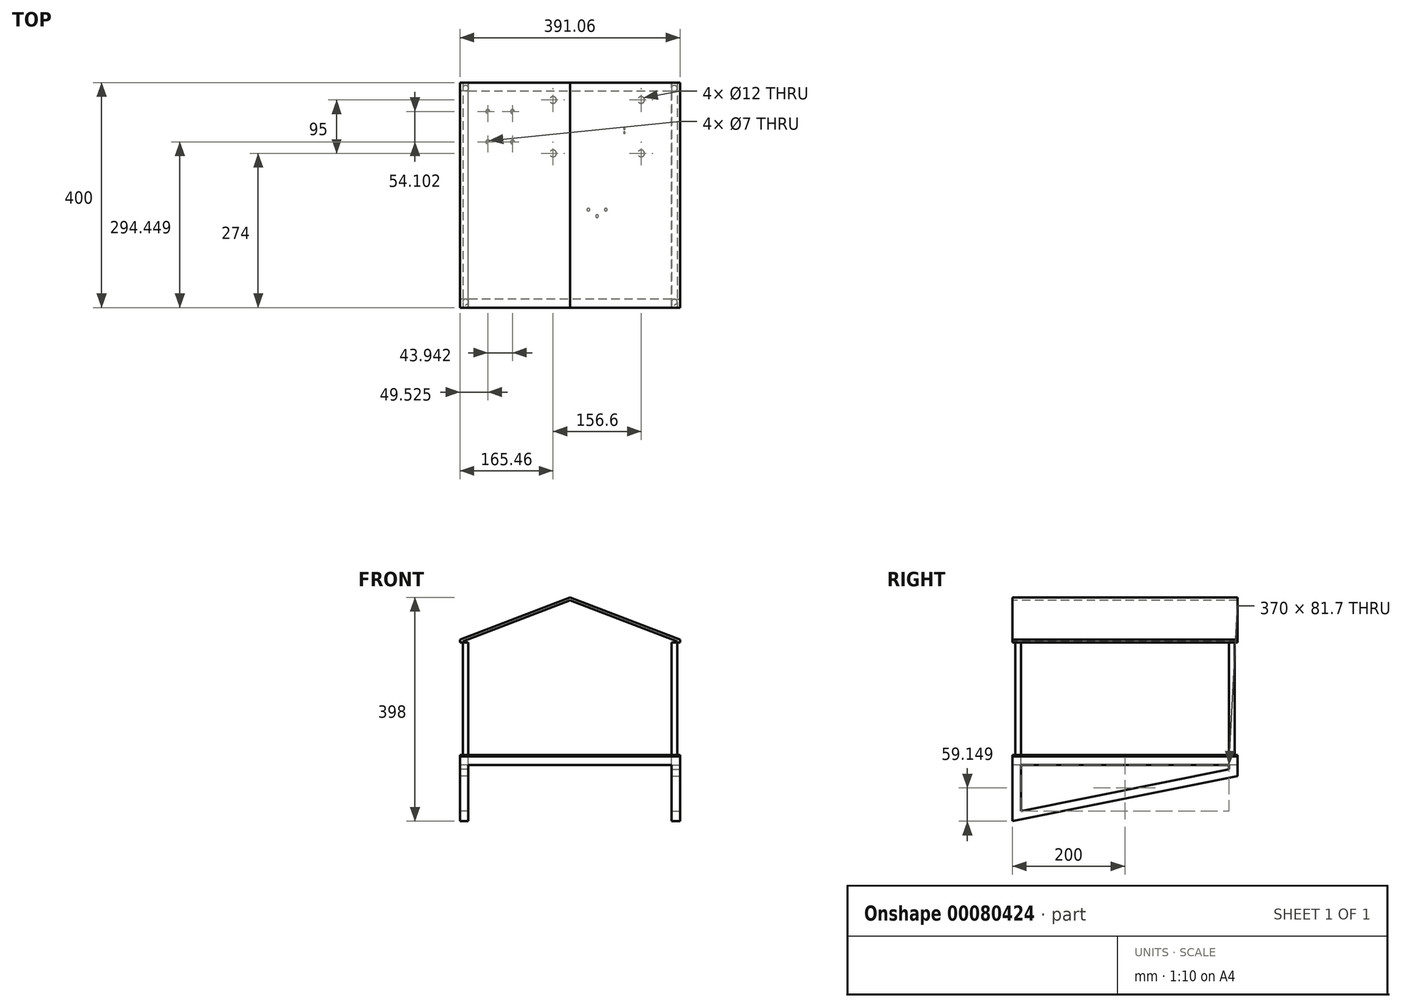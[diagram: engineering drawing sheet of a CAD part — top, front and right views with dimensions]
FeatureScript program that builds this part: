
annotation { "Feature Type Name" : "Feature", "Feature Type Description" : "" }
export const myFeature = defineFeature(function(context is Context, id is Id, definition is map)
    precondition{}
    {
        {
            var Q0;
            Q0=qCreatedBy(makeId("Top.planeOp"),FACE);
            var sketch = newSketch(context, id + "F0", { "sketchPlane" : qUnion([Q0])});
            skLineSegment(sketch, "E0.bottom", {"start": v(-195.53, 200) * mm, "end": v(195.53, 200) * mm});
            skLineSegment(sketch, "E0.top", {"start": v(-195.53, -200) * mm, "end": v(195.53, -200) * mm});
            skLineSegment(sketch, "E0.left", {"start": v(-195.53, 200) * mm, "end": v(-195.53, -200) * mm});
            skLineSegment(sketch, "E0.right", {"start": v(195.53, 200) * mm, "end": v(195.53, -200) * mm});
            skPoint(sketch, "E0.middle", {"position": v(0, 0) * mm});
            skCircle(sketch, "E1", {"center": v(126.53, 169) * mm, "radius": 6 * mm});
            skCircle(sketch, "E2", {"center": v(126.53, 74) * mm, "radius": 6 * mm});
            skLineSegment(sketch, "E3", {"start": v(48.23, 169) * mm, "end": v(48.23, 74) * mm, "construction": true});
            skCircle(sketch, "E4.MirrorC", {"center": v(-30.07, 169) * mm, "radius": 6 * mm});
            skCircle(sketch, "E5.MirrorC", {"center": v(-30.07, 74) * mm, "radius": 6 * mm});
            skLineSegment(sketch, "E6.bottom", {"start": v(107.53, 185) * mm, "end": v(145.53, 185) * mm, "construction": true});
            skLineSegment(sketch, "E6.top", {"start": v(107.53, 58) * mm, "end": v(145.53, 58) * mm, "construction": true});
            skLineSegment(sketch, "E6.left", {"start": v(107.53, 185) * mm, "end": v(107.53, 58) * mm, "construction": true});
            skLineSegment(sketch, "E6.right", {"start": v(145.53, 185) * mm, "end": v(145.53, 58) * mm, "construction": true});
            skPoint(sketch, "E6.middle", {"position": v(126.53, 121.5) * mm});
            skLineSegment(sketch, "E7", {"start": v(126.53, 169) * mm, "end": v(126.53, 74) * mm, "construction": true});
            skCircle(sketch, "E8", {"center": v(-102.06, 148.55) * mm, "radius": 3.5 * mm});
            skCircle(sketch, "E9", {"center": v(-102.06, 94.45) * mm, "radius": 3.5 * mm});
            skLineSegment(sketch, "E10", {"start": v(-124.03, 148.55) * mm, "end": v(-124.03, 94.45) * mm, "construction": true});
            skCircle(sketch, "E11.MirrorC", {"center": v(-146, 148.55) * mm, "radius": 3.5 * mm});
            skCircle(sketch, "E12.MirrorC", {"center": v(-146, 94.45) * mm, "radius": 3.5 * mm});
            skPoint(sketch, "E13", {"position": v(-124.03, 121.5) * mm});
            skLineSegment(sketch, "E14.bottom", {"start": v(-155.53, 161.5) * mm, "end": v(-92.54, 161.5) * mm, "construction": true});
            skLineSegment(sketch, "E14.top", {"start": v(-155.53, 81.5) * mm, "end": v(-92.54, 81.5) * mm, "construction": true});
            skLineSegment(sketch, "E14.left", {"start": v(-155.53, 161.5) * mm, "end": v(-155.53, 81.5) * mm, "construction": true});
            skLineSegment(sketch, "E14.right", {"start": v(-92.54, 161.5) * mm, "end": v(-92.54, 81.5) * mm, "construction": true});
            skCircle(sketch, "E15", {"center": v(32.73, -25.91) * mm, "radius": 2.5 * mm});
            skCircle(sketch, "E16", {"center": v(63.73, -25.91) * mm, "radius": 2.5 * mm});
            skLineSegment(sketch, "E17", {"start": v(32.73, -25.91) * mm, "end": v(63.73, -25.91) * mm, "construction": true});
            skPoint(sketch, "E18", {"position": v(48.23, -25.91) * mm});
            skCircle(sketch, "E19", {"center": v(48.23, -37.5) * mm, "radius": 1.59 * mm, "construction": true});
            skPoint(sketch, "E20", {"position": v(48.23, -35.91) * mm});
            skCircle(sketch, "E21", {"center": v(48.23, -37.5) * mm, "radius": 2.5 * mm});
            skLineSegment(sketch, "E22.bottom", {"start": v(94.23, 122) * mm, "end": v(99.23, 122) * mm, "construction": true});
            skLineSegment(sketch, "E22.top", {"start": v(94.23, 107) * mm, "end": v(99.23, 107) * mm, "construction": true});
            skLineSegment(sketch, "E22.left", {"start": v(94.23, 122) * mm, "end": v(94.23, 107) * mm, "construction": true});
            skLineSegment(sketch, "E22.right", {"start": v(99.23, 122) * mm, "end": v(99.23, 121) * mm, "construction": true});
            skLineSegment(sketch, "E23", {"start": v(94.23, 121) * mm, "end": v(99.23, 121) * mm, "construction": true});
            skLineSegment(sketch, "E24", {"start": v(99.23, 121) * mm, "end": v(99.23, 107) * mm, "construction": true});
            skPoint(sketch, "E25", {"position": v(99.23, 121.5) * mm});
            skCircle(sketch, "E26", {"center": v(96.73, 118) * mm, "radius": 1.5 * mm});
            skPoint(sketch, "E26.centerSnap0", {"position": v(96.73, 122) * mm});
            skCircle(sketch, "E27", {"center": v(96.73, 111) * mm, "radius": 1.5 * mm});
            skLineSegment(sketch, "E28", {"start": v(96.73, 118) * mm, "end": v(96.73, 111) * mm, "construction": true});
            skPoint(sketch, "E29", {"position": v(94.23, 114.5) * mm});
            skPoint(sketch, "E30", {"position": v(96.73, 114.5) * mm});
            skSolve(sketch);
        }
        {
            var Q0;
            Q0 = qSketchRegion(id + "F0", true);
            extrude(context, id + "F1", {"entities" : qUnion([Q0]), "endBound" : BoundingType.SYMMETRIC, "depth" : 3 * mm});
        }
        {
            var Q0;
            Q0=makeQuery(id+"F1.opExtrude","CAP_FACE",FACE,{"disambiguationData":[OSD([sQuery(id+"F0.wireOp",EDGE,"E0.bottom"),sQuery(id+"F0.wireOp",EDGE,"E0.top"),sQuery(id+"F0.wireOp",EDGE,"E0.left"),sQuery(id+"F0.wireOp",EDGE,"E0.right"),sQuery(id+"F0.wireOp",EDGE,"E1"),sQuery(id+"F0.wireOp",EDGE,"E2"),sQuery(id+"F0.wireOp",EDGE,"E4.MirrorC"),sQuery(id+"F0.wireOp",EDGE,"E5.MirrorC"),sQuery(id+"F0.wireOp",EDGE,"E8"),sQuery(id+"F0.wireOp",EDGE,"E9"),sQuery(id+"F0.wireOp",EDGE,"E11.MirrorC"),sQuery(id+"F0.wireOp",EDGE,"E12.MirrorC"),sQuery(id+"F0.wireOp",EDGE,"E15"),sQuery(id+"F0.wireOp",EDGE,"E16"),sQuery(id+"F0.wireOp",EDGE,"E21"),sQuery(id+"F0.wireOp",EDGE,"E26"),sQuery(id+"F0.wireOp",EDGE,"E27")])],"isStart":true});
            var sketch = newSketch(context, id + "F2", { "sketchPlane" : qUnion([Q0])});
            skLineSegment(sketch, "E31.0.0", {"start": v(-195.53, -200) * mm, "end": v(195.53, -200) * mm});
            skLineSegment(sketch, "E31.0.1", {"start": v(195.53, -200) * mm, "end": v(195.53, 200) * mm});
            skLineSegment(sketch, "E31.0.2", {"start": v(195.53, 200) * mm, "end": v(-195.53, 200) * mm});
            skLineSegment(sketch, "E31.0.3", {"start": v(-195.53, 200) * mm, "end": v(-195.53, -200) * mm});
            skLineSegment(sketch, "E32.0", {"start": v(-180.53, -185) * mm, "end": v(180.53, -185) * mm});
            skLineSegment(sketch, "E32.1", {"start": v(-180.53, 185) * mm, "end": v(-180.53, -185) * mm});
            skLineSegment(sketch, "E32.2", {"start": v(180.53, 185) * mm, "end": v(-180.53, 185) * mm});
            skLineSegment(sketch, "E32.3", {"start": v(180.53, -185) * mm, "end": v(180.53, 185) * mm});
            skSolve(sketch);
        }
        {
            var Q0;
            Q0 = qSketchRegion(id + "F2", true);
            extrude(context, id + "F3", {"entities" : qUnion([Q0]), "depth" : 15 * mm});
        }
        {
            var Q0;
            Q0=makeQuery(id+"F3.opExtrude","SWEPT_FACE",FACE,{"disambiguationData":[OSD([sQuery(id+"F2.wireOp",EDGE,"E31.0.1")])]});
            var sketch = newSketch(context, id + "F4", { "sketchPlane" : qUnion([Q0])});
            skLineSegment(sketch, "E33", {"start": v(-200, -16.5) * mm, "end": v(-200, -116.5) * mm});
            skLineSegment(sketch, "E34", {"start": v(-200, -116.5) * mm, "end": v(200, -36.5) * mm});
            skLineSegment(sketch, "E35", {"start": v(200, -36.5) * mm, "end": v(200, -16.5) * mm});
            skLineSegment(sketch, "E36", {"start": v(-185, -16.5) * mm, "end": v(-185, -98.2) * mm});
            skLineSegment(sketch, "E37", {"start": v(-185, -98.2) * mm, "end": v(185, -24.2) * mm});
            skLineSegment(sketch, "E38", {"start": v(185, -24.2) * mm, "end": v(185, -16.5) * mm});
            skLineSegment(sketch, "E39", {"start": v(-200, -16.5) * mm, "end": v(-185, -16.5) * mm});
            skLineSegment(sketch, "E40", {"start": v(200, -16.5) * mm, "end": v(185, -16.5) * mm});
            skSolve(sketch);
        }
        {
            var Q0;
            Q0 = qSketchRegion(id + "F4", true);
            extrude(context, id + "F5", {"entities" : qUnion([Q0]), "oppositeDirection" : true, "depth" : 15 * mm});
        }
        {
            var Q0;
            Q0=makeQuery(id+"F5.opExtrude","SWEPT_BODY",BODY,{"disambiguationData":[OSD([sQuery(id+"F4.wireOp",EDGE,"E33"),sQuery(id+"F4.wireOp",EDGE,"E34"),sQuery(id+"F4.wireOp",EDGE,"E35"),sQuery(id+"F4.wireOp",EDGE,"E36"),sQuery(id+"F4.wireOp",EDGE,"E37"),sQuery(id+"F4.wireOp",EDGE,"E38"),sQuery(id+"F4.wireOp",EDGE,"E39"),sQuery(id+"F4.wireOp",EDGE,"E40")])]});
            var Q1;
            Q1=qCreatedBy(makeId("Right.planeOp"),FACE);
            mirror(context, id + "F6", {"operationType" : NewBodyOperationType.ADD, "entities" : qUnion([Q0]), "mirrorPlane" : qUnion([Q1])});
        }
        {
            var Q0;
            Q0=makeQuery(id+"F1.opExtrude","CAP_FACE",FACE,{"disambiguationData":[OSD([sQuery(id+"F0.wireOp",EDGE,"E0.bottom"),sQuery(id+"F0.wireOp",EDGE,"E0.top"),sQuery(id+"F0.wireOp",EDGE,"E0.left"),sQuery(id+"F0.wireOp",EDGE,"E0.right"),sQuery(id+"F0.wireOp",EDGE,"E1"),sQuery(id+"F0.wireOp",EDGE,"E2"),sQuery(id+"F0.wireOp",EDGE,"E4.MirrorC"),sQuery(id+"F0.wireOp",EDGE,"E5.MirrorC"),sQuery(id+"F0.wireOp",EDGE,"E8"),sQuery(id+"F0.wireOp",EDGE,"E9"),sQuery(id+"F0.wireOp",EDGE,"E11.MirrorC"),sQuery(id+"F0.wireOp",EDGE,"E12.MirrorC"),sQuery(id+"F0.wireOp",EDGE,"E15"),sQuery(id+"F0.wireOp",EDGE,"E16"),sQuery(id+"F0.wireOp",EDGE,"E21"),sQuery(id+"F0.wireOp",EDGE,"E26"),sQuery(id+"F0.wireOp",EDGE,"E27")])],"isStart":false});
            var sketch = newSketch(context, id + "F7", { "sketchPlane" : qUnion([Q0])});
            skCircle(sketch, "E41", {"center": v(-185.53, 190) * mm, "radius": 5 * mm});
            skCircle(sketch, "E42.MirrorC", {"center": v(185.53, 190) * mm, "radius": 5 * mm});
            skCircle(sketch, "E43.MirrorC", {"center": v(185.53, -190) * mm, "radius": 5 * mm});
            skCircle(sketch, "E44.MirrorC", {"center": v(-185.53, -190) * mm, "radius": 5 * mm});
            skSolve(sketch);
        }
        {
            var Q0;
            Q0 = qSketchRegion(id + "F7", true);
            extrude(context, id + "F8", {"entities" : qUnion([Q0]), "operationType" : NewBodyOperationType.ADD, "depth" : 200 * mm});
        }
        {
            var Q0;
            Q0=makeQuery(id+"F8.opExtrude","CAP_FACE",FACE,{"disambiguationData":[OSD([sQuery(id+"F7.wireOp",EDGE,"E41")])],"isStart":false});
            var sketch = newSketch(context, id + "F9", { "sketchPlane" : qUnion([Q0])});
            skLineSegment(sketch, "E45.0", {"start": v(-195.53, 200) * mm, "end": v(195.53, 200) * mm});
            skLineSegment(sketch, "E46.0", {"start": v(-195.53, 200) * mm, "end": v(-195.53, -200) * mm});
            skLineSegment(sketch, "E47.0", {"start": v(-195.53, -200) * mm, "end": v(195.53, -200) * mm});
            skLineSegment(sketch, "E48.0", {"start": v(195.53, 200) * mm, "end": v(195.53, -200) * mm});
            skSolve(sketch);
        }
        {
            var Q0;
            Q0 = qSketchRegion(id + "F9", true);
            extrude(context, id + "F10", {"entities" : qUnion([Q0]), "depth" : 80 * mm});
        }
        {
            var Q0;
            Q0=makeQuery(id+"F10.opExtrude","SWEPT_FACE",FACE,{"disambiguationData":[OSD([sQuery(id+"F9.wireOp",EDGE,"E47.0")])]});
            var sketch = newSketch(context, id + "F11", { "sketchPlane" : qUnion([Q0])});
            skLineSegment(sketch, "E49", {"start": v(-195.53, 206.5) * mm, "end": v(0, 281.5) * mm});
            skLineSegment(sketch, "E50", {"start": v(0, 281.5) * mm, "end": v(195.53, 206.5) * mm});
            skLineSegment(sketch, "E51", {"start": v(195.53, 206.5) * mm, "end": v(195.53, 281.5) * mm});
            skLineSegment(sketch, "E52", {"start": v(195.53, 281.5) * mm, "end": v(0, 281.5) * mm});
            skLineSegment(sketch, "E53", {"start": v(-195.53, 206.5) * mm, "end": v(-195.53, 281.5) * mm});
            skLineSegment(sketch, "E54", {"start": v(-195.53, 281.5) * mm, "end": v(0, 281.5) * mm});
            skSolve(sketch);
        }
        {
            var Q0;
            Q0 = qSketchRegion(id + "F11", true);
            extrude(context, id + "F12", {"entities" : qUnion([Q0]), "operationType" : NewBodyOperationType.REMOVE, "endBound" : BoundingType.UP_TO_NEXT, "oppositeDirection" : true, "depth" : 25 * mm});
        }
        {
            var Q0;
            Q0=makeQuery(id+"F10.opExtrude","CAP_FACE",FACE,{"disambiguationData":[OSD([sQuery(id+"F9.wireOp",EDGE,"E45.0"),sQuery(id+"F9.wireOp",EDGE,"E46.0"),sQuery(id+"F9.wireOp",EDGE,"E47.0"),sQuery(id+"F9.wireOp",EDGE,"E48.0")])],"isStart":true});
            var Q1;
            Q1=makeQuery(id+"F10.opExtrude","SWEPT_FACE",FACE,{"disambiguationData":[OSD([sQuery(id+"F9.wireOp",EDGE,"E45.0")])]});
            var Q2;
            Q2=makeQuery(id+"F10.opExtrude","SWEPT_FACE",FACE,{"disambiguationData":[OSD([sQuery(id+"F9.wireOp",EDGE,"E47.0")])]});
            shell(context, id + "F13", {"entities" : qUnion([Q0, Q1, Q2]), "thickness" : 5 * mm});
        }
    });
